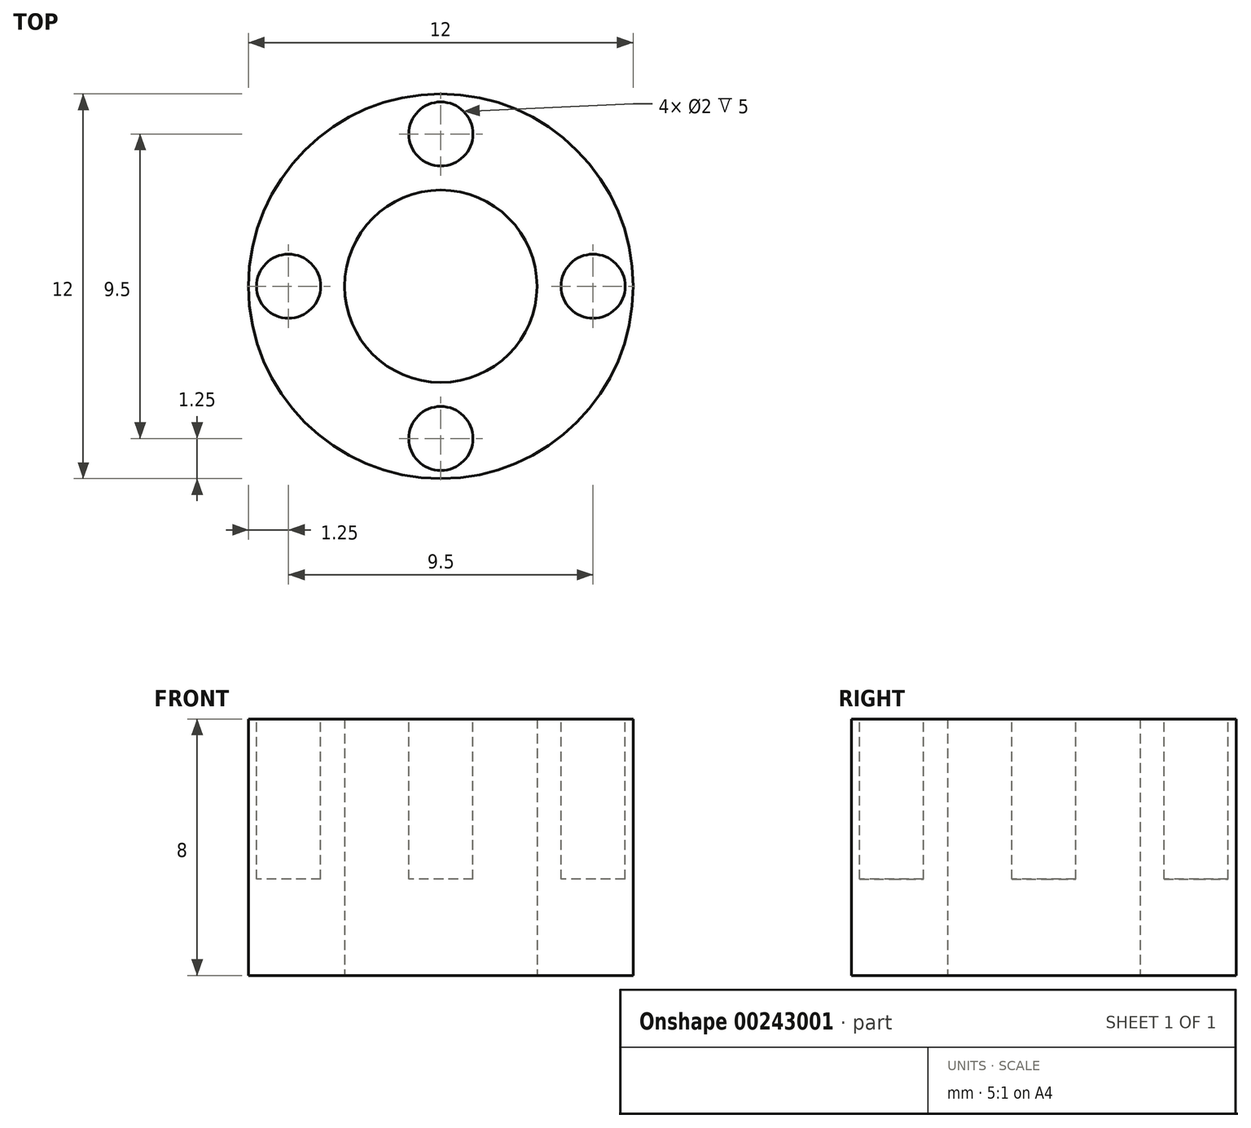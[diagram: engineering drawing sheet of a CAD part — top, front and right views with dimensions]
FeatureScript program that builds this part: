
annotation { "Feature Type Name" : "Feature", "Feature Type Description" : "" }
export const myFeature = defineFeature(function(context is Context, id is Id, definition is map)
    precondition{}
    {
        {
            var Q0;
            Q0=qCreatedBy(makeId("Top.planeOp"),FACE);
            var sketch = newSketch(context, id + "F0", { "sketchPlane" : qUnion([Q0])});
            skCircle(sketch, "E0", {"center": v(0, 0) * mm, "radius": 3 * mm});
            skCircle(sketch, "E1", {"center": v(0, 0) * mm, "radius": 6 * mm});
            skSolve(sketch);
        }
        {
            var Q0;
            Q0 = qSketchRegion(id + "F0", true);
            extrude(context, id + "F1", {"entities" : qUnion([Q0]), "depth" : 8 * mm});
        }
        {
            var Q0;
            Q0=makeQuery(id+"F1.opExtrude","CAP_FACE",FACE,{"disambiguationData":[OSD([sQuery(id+"F0.wireOp",EDGE,"E0"),sQuery(id+"F0.wireOp",EDGE,"E1")])],"isStart":false});
            var sketch = newSketch(context, id + "F2", { "sketchPlane" : qUnion([Q0])});
            skCircle(sketch, "E2", {"center": v(0, 0) * mm, "radius": 4.75 * mm, "construction": true});
            skCircle(sketch, "E3", {"center": v(4.75, 0) * mm, "radius": 1 * mm});
            skCircle(sketch, "E4", {"center": v(0, 4.75) * mm, "radius": 1 * mm});
            skCircle(sketch, "E5", {"center": v(-4.75, 0) * mm, "radius": 1 * mm});
            skCircle(sketch, "E6", {"center": v(0, -4.75) * mm, "radius": 1 * mm});
            skSolve(sketch);
        }
        {
            var Q0;
            Q0 = qSketchRegion(id + "F2", true);
            extrude(context, id + "F3", {"entities" : qUnion([Q0]), "operationType" : NewBodyOperationType.REMOVE, "oppositeDirection" : true, "depth" : 5 * mm});
        }
    });
